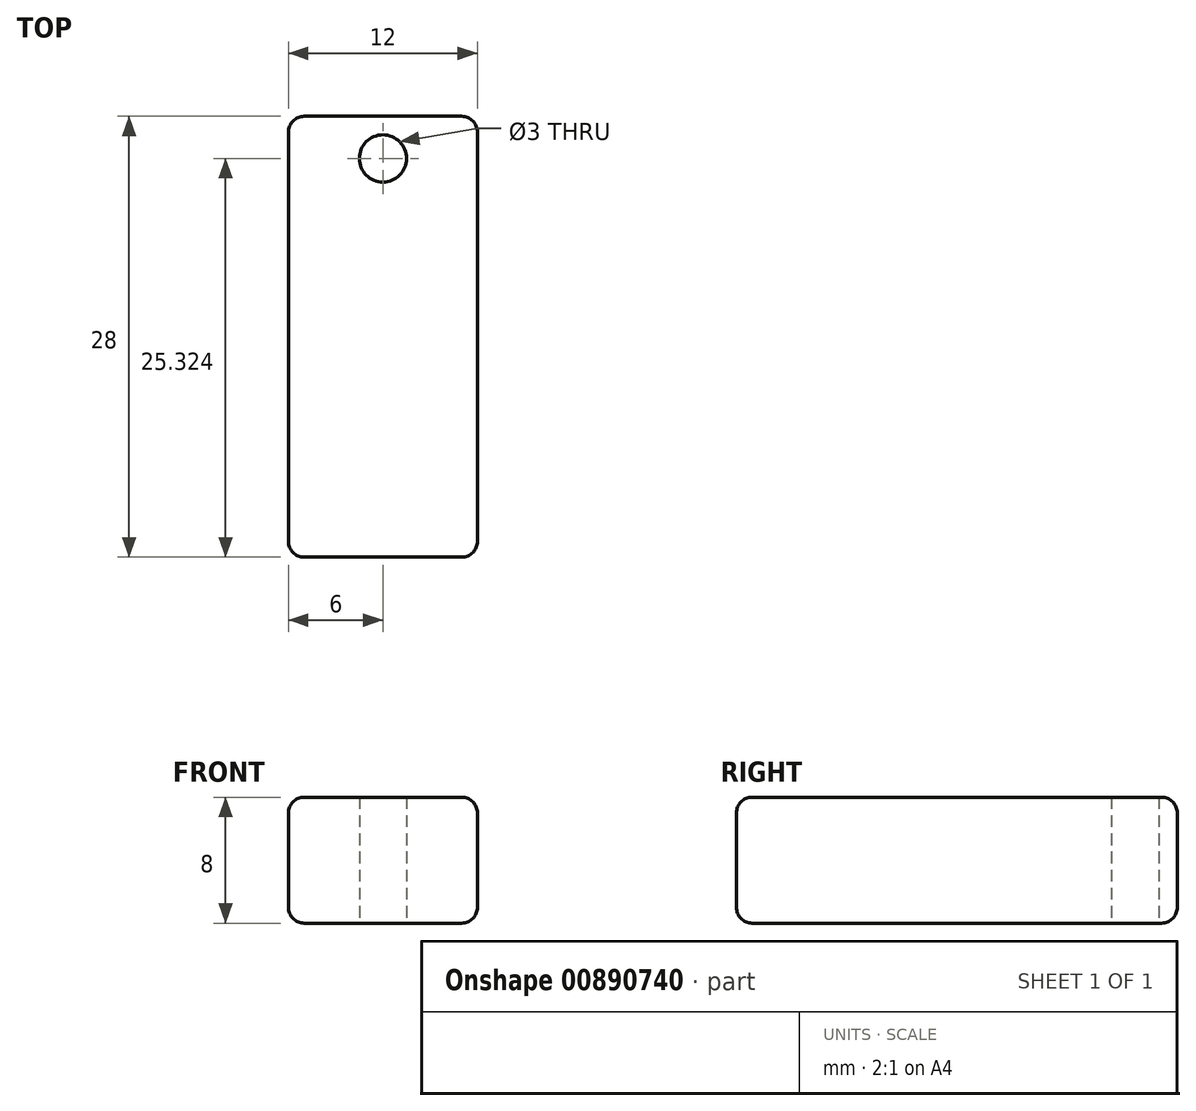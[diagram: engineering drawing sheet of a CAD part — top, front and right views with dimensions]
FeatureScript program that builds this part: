
annotation { "Feature Type Name" : "Feature", "Feature Type Description" : "" }
export const myFeature = defineFeature(function(context is Context, id is Id, definition is map)
    precondition{}
    {
        {
            var Q0;
            Q0=qCreatedBy(makeId("Top.planeOp"),FACE);
            var sketch = newSketch(context, id + "F0", { "sketchPlane" : qUnion([Q0])});
            skLineSegment(sketch, "E0.bottom", {"start": v(6, -14) * mm, "end": v(-6, -14) * mm});
            skLineSegment(sketch, "E0.top", {"start": v(6, 14) * mm, "end": v(-6, 14) * mm});
            skLineSegment(sketch, "E0.left", {"start": v(6, -14) * mm, "end": v(6, 14) * mm});
            skLineSegment(sketch, "E0.right", {"start": v(-6, -14) * mm, "end": v(-6, 14) * mm});
            skPoint(sketch, "E0.middle", {"position": v(0, 0) * mm});
            skCircle(sketch, "E1", {"center": v(0, 11.32) * mm, "radius": 1.5 * mm});
            skPoint(sketch, "E1.centerSnap0", {"position": v(0, 14) * mm});
            skSolve(sketch);
        }
        {
            var Q0;
            Q0 = qSketchRegion(id + "F0", true);
            extrude(context, id + "F1", {"entities" : qUnion([Q0]), "depth" : 8 * mm, "offsetDistance" : 25 * mm});
        }
        {
            var Q0;
            Q0=makeQuery(id+"F1.opExtrude","CAP_EDGE",EDGE,{"disambiguationData":[OSD([sQuery(id+"F0.wireOp",EDGE,"E0.top")])],"isStart":false});
            var Q1;
            Q1=makeQuery(id+"F1.opExtrude","CAP_EDGE",EDGE,{"disambiguationData":[OSD([sQuery(id+"F0.wireOp",EDGE,"E0.left")])],"isStart":false});
            var Q2;
            Q2=makeQuery(id+"F1.opExtrude","CAP_EDGE",EDGE,{"disambiguationData":[OSD([sQuery(id+"F0.wireOp",EDGE,"E0.right")])],"isStart":false});
            var Q3;
            Q3=makeQuery(id+"F1.opExtrude","CAP_EDGE",EDGE,{"disambiguationData":[OSD([sQuery(id+"F0.wireOp",EDGE,"E0.bottom")])],"isStart":false});
            var Q4;
            Q4=makeQuery(id+"F1.opExtrude","SWEPT_EDGE",EDGE,{"disambiguationData":[OSD([sQuery(id+"F0.wireOp",EDGE,"E0.top"),sQuery(id+"F0.wireOp",EDGE,"E0.left")])]});
            var Q5;
            Q5=makeQuery(id+"F1.opExtrude","SWEPT_EDGE",EDGE,{"disambiguationData":[OSD([sQuery(id+"F0.wireOp",EDGE,"E0.top"),sQuery(id+"F0.wireOp",EDGE,"E0.right")])]});
            var Q6;
            Q6=makeQuery(id+"F1.opExtrude","CAP_EDGE",EDGE,{"disambiguationData":[OSD([sQuery(id+"F0.wireOp",EDGE,"E0.top")])],"isStart":true});
            var Q7;
            Q7=makeQuery(id+"F1.opExtrude","CAP_EDGE",EDGE,{"disambiguationData":[OSD([sQuery(id+"F0.wireOp",EDGE,"E0.left")])],"isStart":true});
            var Q8;
            Q8=makeQuery(id+"F1.opExtrude","CAP_EDGE",EDGE,{"disambiguationData":[OSD([sQuery(id+"F0.wireOp",EDGE,"E0.right")])],"isStart":true});
            var Q9;
            Q9=makeQuery(id+"F1.opExtrude","CAP_EDGE",EDGE,{"disambiguationData":[OSD([sQuery(id+"F0.wireOp",EDGE,"E0.bottom")])],"isStart":true});
            var Q10;
            Q10=makeQuery(id+"F1.opExtrude","SWEPT_EDGE",EDGE,{"disambiguationData":[OSD([sQuery(id+"F0.wireOp",EDGE,"E0.bottom"),sQuery(id+"F0.wireOp",EDGE,"E0.left")])]});
            var Q11;
            Q11=makeQuery(id+"F1.opExtrude","SWEPT_EDGE",EDGE,{"disambiguationData":[OSD([sQuery(id+"F0.wireOp",EDGE,"E0.bottom"),sQuery(id+"F0.wireOp",EDGE,"E0.right")])]});
            fillet(context, id + "F2", {"entities" : qUnion([Q0, Q1, Q2, Q3, Q4, Q5, Q6, Q7, Q8, Q9, Q10, Q11]), "radius" : 1 * mm, "tangentPropagation" : true, "allowEdgeOverflow" : false});
        }
    });
